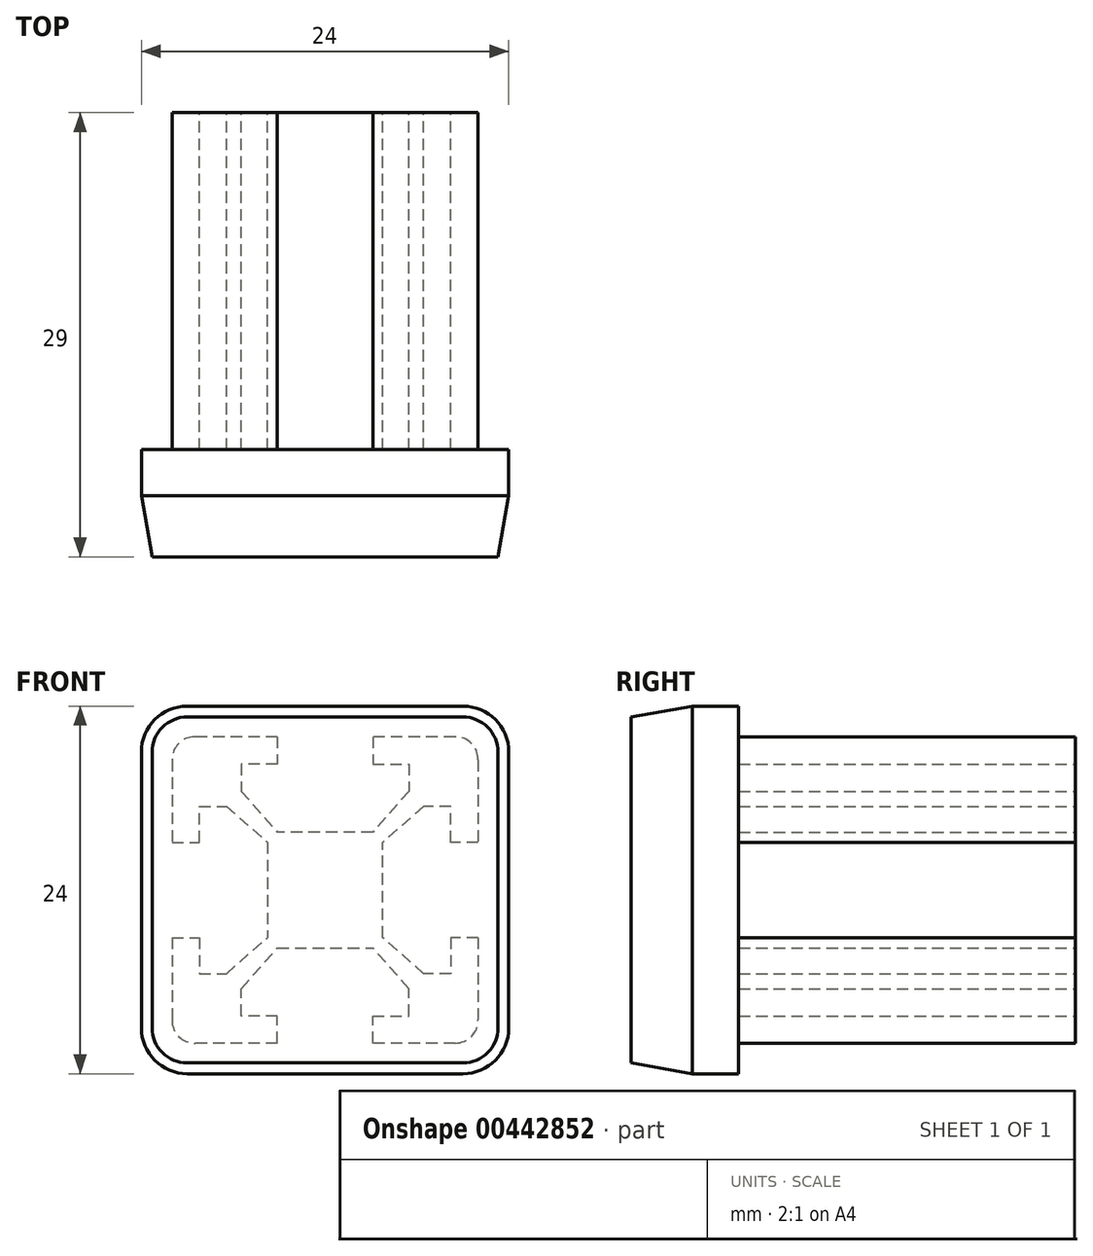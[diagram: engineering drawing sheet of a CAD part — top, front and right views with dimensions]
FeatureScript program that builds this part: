
annotation { "Feature Type Name" : "Feature", "Feature Type Description" : "" }
export const myFeature = defineFeature(function(context is Context, id is Id, definition is map)
    precondition{}
    {
        {
            var Q0;
            Q0=qCreatedBy(makeId("Front.planeOp"),FACE);
            var sketch = newSketch(context, id + "F0", { "sketchPlane" : qUnion([Q0])});
            skLineSegment(sketch, "E0.bottom", {"start": v(10, 10) * mm, "end": v(-10, 10) * mm});
            skLineSegment(sketch, "E0.top", {"start": v(10, -10) * mm, "end": v(-10, -10) * mm});
            skLineSegment(sketch, "E0.left", {"start": v(10, 10) * mm, "end": v(10, -10) * mm});
            skLineSegment(sketch, "E0.right", {"start": v(-10, 10) * mm, "end": v(-10, -10) * mm});
            skPoint(sketch, "E0.middle", {"position": v(0, 0) * mm});
            skLineSegment(sketch, "E1", {"start": v(3.11, 10) * mm, "end": v(3.11, 8.22) * mm});
            skLineSegment(sketch, "E2", {"start": v(3.11, 8.22) * mm, "end": v(5.46, 8.22) * mm});
            skLineSegment(sketch, "E3", {"start": v(5.46, 8.22) * mm, "end": v(5.46, 6.44) * mm});
            skLineSegment(sketch, "E4", {"start": v(5.46, 6.44) * mm, "end": v(3.11, 3.78) * mm});
            skLineSegment(sketch, "E5", {"start": v(3.11, 3.78) * mm, "end": v(0, 3.78) * mm});
            skLineSegment(sketch, "E6.MirrorCS", {"start": v(-3.11, 3.78) * mm, "end": v(0, 3.78) * mm});
            skLineSegment(sketch, "E7.MirrorCS", {"start": v(-5.46, 6.44) * mm, "end": v(-3.11, 3.78) * mm});
            skLineSegment(sketch, "E8.MirrorCS", {"start": v(-3.11, 10) * mm, "end": v(-3.11, 8.22) * mm});
            skLineSegment(sketch, "E9.MirrorCS", {"start": v(-5.46, 8.22) * mm, "end": v(-5.46, 6.44) * mm});
            skLineSegment(sketch, "E10.MirrorCS", {"start": v(-3.11, 8.22) * mm, "end": v(-5.46, 8.22) * mm});
            skLineSegment(sketch, "E11.1.0", {"start": v(-10, 3.11) * mm, "end": v(-8.22, 3.11) * mm});
            skLineSegment(sketch, "E11.1.1", {"start": v(-8.22, 3.11) * mm, "end": v(-8.22, 5.46) * mm});
            skLineSegment(sketch, "E11.1.2", {"start": v(-8.22, 5.46) * mm, "end": v(-6.44, 5.46) * mm});
            skLineSegment(sketch, "E11.1.3", {"start": v(-6.44, 5.46) * mm, "end": v(-3.78, 3.11) * mm});
            skLineSegment(sketch, "E11.1.4", {"start": v(-3.78, 3.11) * mm, "end": v(-3.78, 0) * mm});
            skLineSegment(sketch, "E11.1.5", {"start": v(-3.78, -3.11) * mm, "end": v(-3.78, 0) * mm});
            skLineSegment(sketch, "E11.1.6", {"start": v(-6.44, -5.46) * mm, "end": v(-3.78, -3.11) * mm});
            skLineSegment(sketch, "E11.1.7", {"start": v(-10, -3.11) * mm, "end": v(-8.22, -3.11) * mm});
            skLineSegment(sketch, "E11.1.8", {"start": v(-8.22, -5.46) * mm, "end": v(-6.44, -5.46) * mm});
            skLineSegment(sketch, "E11.1.9", {"start": v(-8.22, -3.11) * mm, "end": v(-8.22, -5.46) * mm});
            skLineSegment(sketch, "E11.2.0", {"start": v(-3.11, -10) * mm, "end": v(-3.11, -8.22) * mm});
            skLineSegment(sketch, "E11.2.1", {"start": v(-3.11, -8.22) * mm, "end": v(-5.46, -8.22) * mm});
            skLineSegment(sketch, "E11.2.2", {"start": v(-5.46, -8.22) * mm, "end": v(-5.46, -6.44) * mm});
            skLineSegment(sketch, "E11.2.3", {"start": v(-5.46, -6.44) * mm, "end": v(-3.11, -3.78) * mm});
            skLineSegment(sketch, "E11.2.4", {"start": v(-3.11, -3.78) * mm, "end": v(0, -3.78) * mm});
            skLineSegment(sketch, "E11.2.5", {"start": v(3.11, -3.78) * mm, "end": v(0, -3.78) * mm});
            skLineSegment(sketch, "E11.2.6", {"start": v(5.46, -6.44) * mm, "end": v(3.11, -3.78) * mm});
            skLineSegment(sketch, "E11.2.7", {"start": v(3.11, -10) * mm, "end": v(3.11, -8.22) * mm});
            skLineSegment(sketch, "E11.2.8", {"start": v(5.46, -8.22) * mm, "end": v(5.46, -6.44) * mm});
            skLineSegment(sketch, "E11.2.9", {"start": v(3.11, -8.22) * mm, "end": v(5.46, -8.22) * mm});
            skLineSegment(sketch, "E11.3.0", {"start": v(10, -3.11) * mm, "end": v(8.22, -3.11) * mm});
            skLineSegment(sketch, "E11.3.1", {"start": v(8.22, -3.11) * mm, "end": v(8.22, -5.46) * mm});
            skLineSegment(sketch, "E11.3.2", {"start": v(8.22, -5.46) * mm, "end": v(6.44, -5.46) * mm});
            skLineSegment(sketch, "E11.3.3", {"start": v(6.44, -5.46) * mm, "end": v(3.78, -3.11) * mm});
            skLineSegment(sketch, "E11.3.4", {"start": v(3.78, -3.11) * mm, "end": v(3.78, 0) * mm});
            skLineSegment(sketch, "E11.3.5", {"start": v(3.78, 3.11) * mm, "end": v(3.78, 0) * mm});
            skLineSegment(sketch, "E11.3.6", {"start": v(6.44, 5.46) * mm, "end": v(3.78, 3.11) * mm});
            skLineSegment(sketch, "E11.3.7", {"start": v(10, 3.11) * mm, "end": v(8.22, 3.11) * mm});
            skLineSegment(sketch, "E11.3.8", {"start": v(8.22, 5.46) * mm, "end": v(6.44, 5.46) * mm});
            skLineSegment(sketch, "E11.3.9", {"start": v(8.22, 3.11) * mm, "end": v(8.22, 5.46) * mm});
            skSolve(sketch);
        }
        {
            var Q0;
            {var subQ12=sQuery(id+"F0.wireOp",EDGE,"E1");Q0=makeQuery(id+"F0.imprint","IMPRINT",FACE,{"disambiguationData":[TD([[makeQuery(id+"F0.imprint","IMPRINT",EDGE,{"derivedFrom":subQ12}),1.0]])]});}
            extrude(context, id + "F1", {"entities" : qUnion([Q0]), "depth" : 25 * mm});
        }
        {
            var Q0;
            Q0=makeQuery(id+"F1.opExtrude","SWEPT_EDGE",EDGE,{"disambiguationData":[OSD([sQuery(id+"F0.wireOp",EDGE,"E0.bottom"),sQuery(id+"F0.wireOp",EDGE,"E0.right")])]});
            var Q1;
            Q1=makeQuery(id+"F1.opExtrude","SWEPT_EDGE",EDGE,{"disambiguationData":[OSD([sQuery(id+"F0.wireOp",EDGE,"E0.bottom"),sQuery(id+"F0.wireOp",EDGE,"E0.left")])]});
            var Q2;
            Q2=makeQuery(id+"F1.opExtrude","SWEPT_EDGE",EDGE,{"disambiguationData":[OSD([sQuery(id+"F0.wireOp",EDGE,"E0.top"),sQuery(id+"F0.wireOp",EDGE,"E0.left")])]});
            var Q3;
            Q3=makeQuery(id+"F1.opExtrude","SWEPT_EDGE",EDGE,{"disambiguationData":[OSD([sQuery(id+"F0.wireOp",EDGE,"E0.top"),sQuery(id+"F0.wireOp",EDGE,"E0.right")])]});
            fillet(context, id + "F2", {"entities" : qUnion([Q0, Q1, Q2, Q3]), "radius" : 1.5 * mm, "tangentPropagation" : true, "allowEdgeOverflow" : false});
        }
        {
            var Q0;
            Q0=makeQuery(id+"F1.opExtrude","CAP_FACE",FACE,{"disambiguationData":[OSD([sQuery(id+"F0.wireOp",EDGE,"E0.bottom"),sQuery(id+"F0.wireOp",EDGE,"E0.top"),sQuery(id+"F0.wireOp",EDGE,"E0.left"),sQuery(id+"F0.wireOp",EDGE,"E0.right"),sQuery(id+"F0.wireOp",EDGE,"E1"),sQuery(id+"F0.wireOp",EDGE,"E2"),sQuery(id+"F0.wireOp",EDGE,"E3"),sQuery(id+"F0.wireOp",EDGE,"E4"),sQuery(id+"F0.wireOp",EDGE,"E5"),sQuery(id+"F0.wireOp",EDGE,"E6.MirrorCS"),sQuery(id+"F0.wireOp",EDGE,"E7.MirrorCS"),sQuery(id+"F0.wireOp",EDGE,"E8.MirrorCS"),sQuery(id+"F0.wireOp",EDGE,"E9.MirrorCS"),sQuery(id+"F0.wireOp",EDGE,"E10.MirrorCS"),sQuery(id+"F0.wireOp",EDGE,"E11.1.0"),sQuery(id+"F0.wireOp",EDGE,"E11.1.1"),sQuery(id+"F0.wireOp",EDGE,"E11.1.2"),sQuery(id+"F0.wireOp",EDGE,"E11.1.3"),sQuery(id+"F0.wireOp",EDGE,"E11.1.4"),sQuery(id+"F0.wireOp",EDGE,"E11.1.5"),sQuery(id+"F0.wireOp",EDGE,"E11.1.6"),sQuery(id+"F0.wireOp",EDGE,"E11.1.7"),sQuery(id+"F0.wireOp",EDGE,"E11.1.8"),sQuery(id+"F0.wireOp",EDGE,"E11.1.9"),sQuery(id+"F0.wireOp",EDGE,"E11.2.0"),sQuery(id+"F0.wireOp",EDGE,"E11.2.1"),sQuery(id+"F0.wireOp",EDGE,"E11.2.2"),sQuery(id+"F0.wireOp",EDGE,"E11.2.3"),sQuery(id+"F0.wireOp",EDGE,"E11.2.4"),sQuery(id+"F0.wireOp",EDGE,"E11.2.5"),sQuery(id+"F0.wireOp",EDGE,"E11.2.6"),sQuery(id+"F0.wireOp",EDGE,"E11.2.7"),sQuery(id+"F0.wireOp",EDGE,"E11.2.8"),sQuery(id+"F0.wireOp",EDGE,"E11.2.9"),sQuery(id+"F0.wireOp",EDGE,"E11.3.0"),sQuery(id+"F0.wireOp",EDGE,"E11.3.1"),sQuery(id+"F0.wireOp",EDGE,"E11.3.2"),sQuery(id+"F0.wireOp",EDGE,"E11.3.3"),sQuery(id+"F0.wireOp",EDGE,"E11.3.4"),sQuery(id+"F0.wireOp",EDGE,"E11.3.5"),sQuery(id+"F0.wireOp",EDGE,"E11.3.6"),sQuery(id+"F0.wireOp",EDGE,"E11.3.7"),sQuery(id+"F0.wireOp",EDGE,"E11.3.8"),sQuery(id+"F0.wireOp",EDGE,"E11.3.9")])],"isStart":false});
            var sketch = newSketch(context, id + "F3", { "sketchPlane" : qUnion([Q0])});
            skLineSegment(sketch, "E12.bottom", {"start": v(-9, 12) * mm, "end": v(9, 12) * mm});
            skLineSegment(sketch, "E12.top", {"start": v(-9, -12) * mm, "end": v(9, -12) * mm});
            skLineSegment(sketch, "E12.left", {"start": v(-12, 9) * mm, "end": v(-12, -9) * mm});
            skLineSegment(sketch, "E12.right", {"start": v(12, 9) * mm, "end": v(12, -9) * mm});
            skPoint(sketch, "E13.visualSharp", {"position": v(-12, 12) * mm});
            skArc(sketch, "E13.filletArc", {"start": v(-9, 12) * mm, "mid": v(-11.12, 11.12) * mm, "end": v(-12, 9) * mm});
            skPoint(sketch, "E14.visualSharp", {"position": v(12, 12) * mm});
            skArc(sketch, "E14.filletArc", {"start": v(12, 9) * mm, "mid": v(11.12, 11.12) * mm, "end": v(9, 12) * mm});
            skPoint(sketch, "E15.visualSharp", {"position": v(12, -12) * mm});
            skArc(sketch, "E15.filletArc", {"start": v(9, -12) * mm, "mid": v(11.12, -11.12) * mm, "end": v(12, -9) * mm});
            skPoint(sketch, "E16.visualSharp", {"position": v(-12, -12) * mm});
            skArc(sketch, "E16.filletArc", {"start": v(-12, -9) * mm, "mid": v(-11.12, -11.12) * mm, "end": v(-9, -12) * mm});
            skSolve(sketch);
        }
        {
            var Q0;
            Q0=makeQuery(id+"F3.imprint","IMPRINT",FACE,{"disambiguationData":[TD([[makeQuery(id+"F3.imprint","IMPRINT",EDGE,{"derivedFrom":sQuery(id+"F3.wireOp",EDGE,"E12.bottom")}),-1.0]])]});
            var Q1;
            {var subQ13=sQuery(id+"F0.wireOp",EDGE,"E1");Q1=makeQuery(id+"F3.imprint","IMPRINT",FACE,{"disambiguationData":[TD([[makeQuery(id+"F3.imprint","IMPRINT",EDGE,{"derivedFrom":makeQuery(id+"F1.opExtrude","CAP_EDGE",EDGE,{"disambiguationData":[OSD([subQ13])],"isStart":false})}),1.0]])]});}
            extrude(context, id + "F4", {"entities" : qUnion([Q0, Q1]), "depth" : 4 * mm, "hasDraft" : true, "draftAngle" : 10 * degree, "draftPullDirection" : true});
        }
        {
            var Q0;
            Q0=makeQuery(id+"F3.imprint","IMPRINT",FACE,{"disambiguationData":[TD([[makeQuery(id+"F3.imprint","IMPRINT",EDGE,{"derivedFrom":sQuery(id+"F3.wireOp",EDGE,"E12.bottom")}),-1.0]])]});
            extrude(context, id + "F5", {"entities" : qUnion([Q0]), "operationType" : NewBodyOperationType.ADD, "oppositeDirection" : true, "depth" : 3 * mm});
        }
    });
